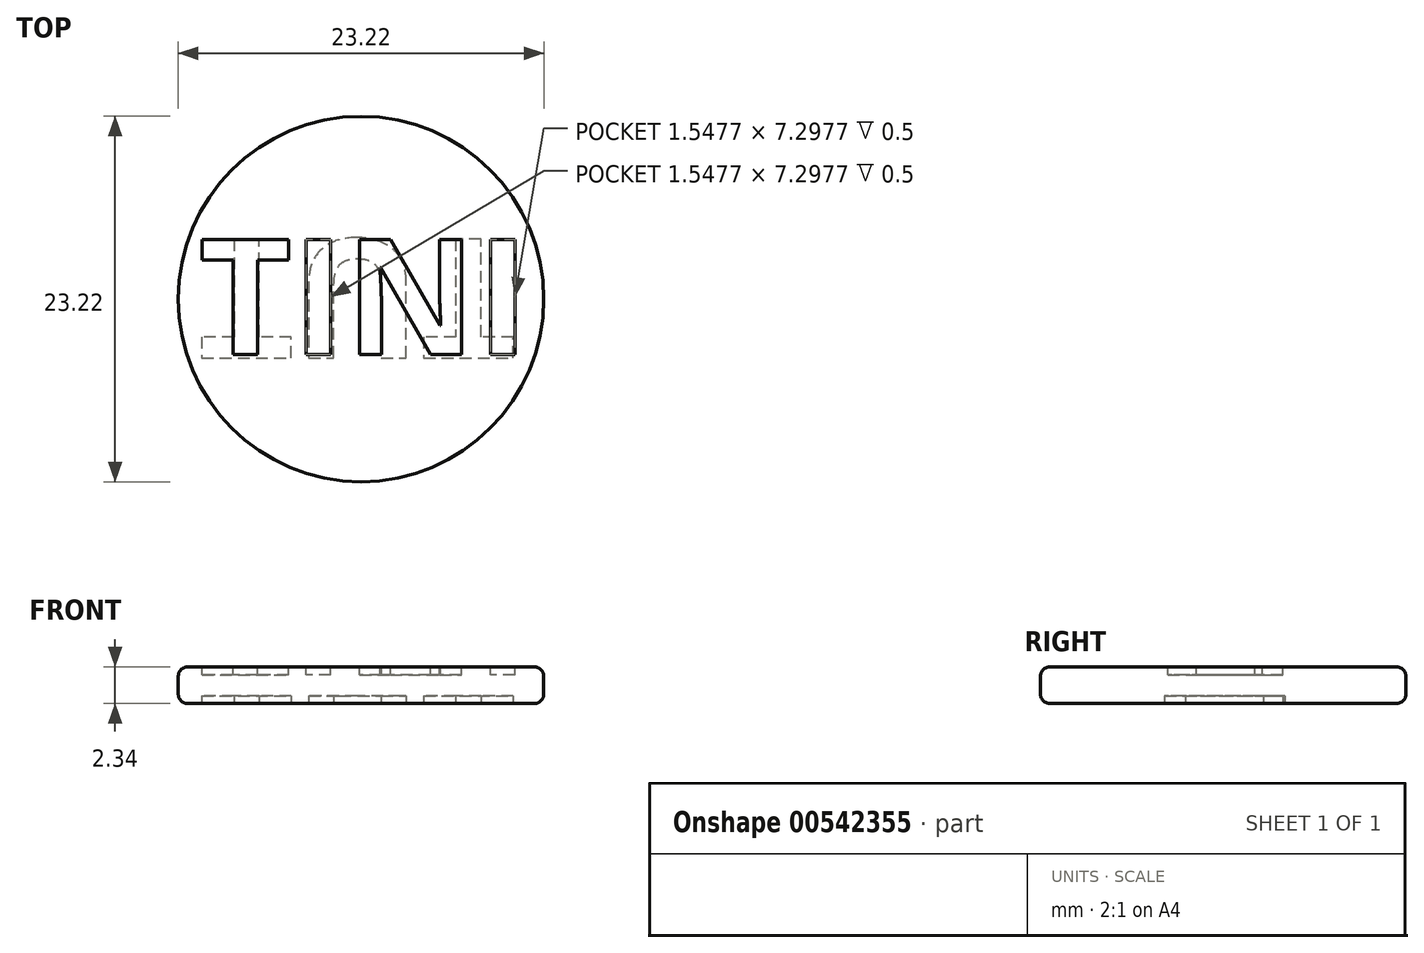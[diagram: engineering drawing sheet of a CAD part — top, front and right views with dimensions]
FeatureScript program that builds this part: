
annotation { "Feature Type Name" : "Feature", "Feature Type Description" : "" }
export const myFeature = defineFeature(function(context is Context, id is Id, definition is map)
    precondition{}
    {
        {
            var Q0;
            Q0=qCreatedBy(makeId("Top.planeOp"),FACE);
            var sketch = newSketch(context, id + "F0", { "sketchPlane" : qUnion([Q0])});
            skCircle(sketch, "E0", {"center": v(0, 0) * mm, "radius": 11.6 * mm});
            skSolve(sketch);
        }
        {
            var Q0;
            Q0 = qSketchRegion(id + "F0", true);
            extrude(context, id + "F1", {"entities" : qUnion([Q0]), "endBound" : BoundingType.SYMMETRIC, "depth" : 2.33 * mm, "offsetDistance" : 25 * mm});
        }
        {
            var Q0;
            Q0=makeQuery(id+"F1.opExtrude","SWEPT_FACE",FACE,{"disambiguationData":[OSD([sQuery(id+"F0.wireOp",EDGE,"E0")])]});
            var Q1;
            Q1=makeQuery(id+"F1.opExtrude","CAP_EDGE",EDGE,{"disambiguationData":[OSD([sQuery(id+"F0.wireOp",EDGE,"E0")])],"isStart":true});
            fillet(context, id + "F2", {"entities" : qUnion([Q0, Q1]), "radius" : 0.6 * mm, "tangentPropagation" : true, "allowEdgeOverflow" : false});
        }
        {
            var Q0;
            Q0=makeQuery(id+"F1.opExtrude","CAP_FACE",FACE,{"disambiguationData":[OSD([sQuery(id+"F0.wireOp",EDGE,"E0")])],"isStart":false});
            var sketch = newSketch(context, id + "F3", { "sketchPlane" : qUnion([Q0])});
            skText(sketch, "E1", { "text": "TINI", "fontName": "OpenSans-Bold.ttf"});
            const initialGuessF3  = {"E1": [-0.01031, -0.00352, 1, 0, 0.00736]};
            skSetInitialGuess(sketch, initialGuessF3);
            skSolve(sketch);
        }
        {
            var Q0;
            Q0 = qSketchRegion(id + "F3", true);
            extrude(context, id + "F4", {"entities" : qUnion([Q0]), "operationType" : NewBodyOperationType.REMOVE, "oppositeDirection" : true, "depth" : 0.5 * mm, "offsetDistance" : 25 * mm});
        }
        {
            var Q0;
            Q0=makeQuery(id+"F1.opExtrude","CAP_FACE",FACE,{"disambiguationData":[OSD([sQuery(id+"F0.wireOp",EDGE,"E0")])],"isStart":true});
            var sketch = newSketch(context, id + "F5", { "sketchPlane" : qUnion([Q0])});
            skText(sketch, "E2", { "text": "TUT", "fontName": "OpenSans-Bold.ttf"});
            const initialGuessF5  = {"E2": [-0.01033, -0.0038, 1, 0, 0.0076]};
            skSetInitialGuess(sketch, initialGuessF5);
            skSolve(sketch);
        }
        {
            var Q0;
            Q0 = qSketchRegion(id + "F5", true);
            extrude(context, id + "F6", {"entities" : qUnion([Q0]), "operationType" : NewBodyOperationType.REMOVE, "oppositeDirection" : true, "depth" : 0.5 * mm, "offsetDistance" : 25 * mm});
        }
    });
